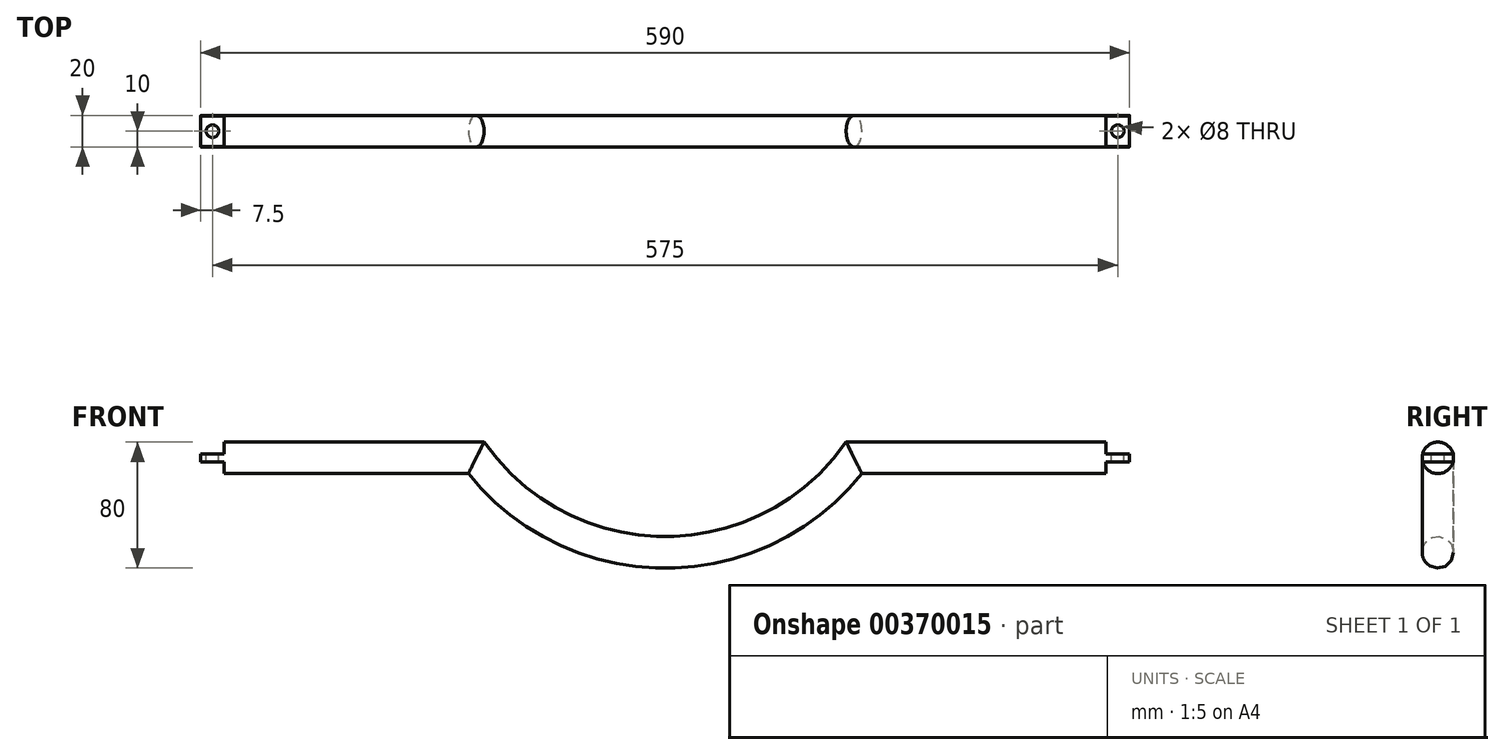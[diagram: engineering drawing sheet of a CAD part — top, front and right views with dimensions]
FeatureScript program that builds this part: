
annotation { "Feature Type Name" : "Feature", "Feature Type Description" : "" }
export const myFeature = defineFeature(function(context is Context, id is Id, definition is map)
    precondition{}
    {
        {
            var Q0;
            Q0=qCreatedBy(makeId("Front.planeOp"),FACE);
            var sketch = newSketch(context, id + "F0", { "sketchPlane" : qUnion([Q0])});
            skPoint(sketch, "E0", {"position": v(-175, 0) * mm});
            skPoint(sketch, "E1", {"position": v(-731.68, -351.24) * mm});
            skPoint(sketch, "E2", {"position": v(-590, 0) * mm});
            skPoint(sketch, "E3", {"position": v(-415, 0) * mm});
            skPoint(sketch, "E4", {"position": v(-295, -60) * mm});
            skLineSegment(sketch, "E5", {"start": v(-590, 0) * mm, "end": v(-415, 0) * mm});
            skLineSegment(sketch, "E6", {"start": v(-175, 0) * mm, "end": v(0, 0) * mm});
            skArc(sketch, "E7", {"start": v(-415, 0) * mm, "mid": v(-295, -60) * mm, "end": v(-175, 0) * mm});
            skSolve(sketch);
        }
        {
            var Q0;
            Q0=qCreatedBy(makeId("Right.planeOp"),FACE);
            var sketch = newSketch(context, id + "F1", { "sketchPlane" : qUnion([Q0])});
            skCircle(sketch, "E8", {"center": v(0, 0) * mm, "radius": 10 * mm});
            skSolve(sketch);
        }
        {
            var Q0;
            Q0=makeQuery(id+"F1.imprint","IMPRINT",FACE,{"disambiguationData":[TD([[makeQuery(id+"F1.imprint","IMPRINT",EDGE,{"derivedFrom":sQuery(id+"F1.wireOp",EDGE,"E8")}),1.0]])]});
            var Q1;
            Q1=sQuery(id+"F0.wireOp",EDGE,"E6");
            var Q2;
            Q2=sQuery(id+"F0.wireOp",EDGE,"E7");
            var Q3;
            Q3=sQuery(id+"F0.wireOp",EDGE,"E5");
            sweep(context, id + "F2", {"profiles" : qUnion([Q0]), "path" : qUnion([Q1, Q2, Q3])});
        }
        {
            var Q0;
            Q0=qCreatedBy(makeId("Front.planeOp"),FACE);
            cPlane(context, id + "F3", {"entities" : qUnion([Q0]), "cplaneType" : CPlaneType.OFFSET, "offset" : 10 * mm, "width" : 150 * mm, "height" : 150 * mm});
        }
        {
            var Q0;
            Q0=qCreatedBy(id+"F3.planeOp",FACE);
            var sketch = newSketch(context, id + "F4", { "sketchPlane" : qUnion([Q0])});
            skLineSegment(sketch, "E9.0", {"start": v(0, -10) * mm, "end": v(0, 10) * mm});
            skLineSegment(sketch, "E10", {"start": v(0, 10) * mm, "end": v(-15, 10) * mm});
            skLineSegment(sketch, "E11", {"start": v(-15, 10) * mm, "end": v(-15, -10) * mm});
            skLineSegment(sketch, "E12", {"start": v(-15, -10) * mm, "end": v(0, -10) * mm});
            skLineSegment(sketch, "E13", {"start": v(0, 0) * mm, "end": v(0, -2.5) * mm});
            skLineSegment(sketch, "E14", {"start": v(0, -2.5) * mm, "end": v(-15, -2.5) * mm});
            skLineSegment(sketch, "E15", {"start": v(-15, -2.5) * mm, "end": v(-15, 2.5) * mm});
            skLineSegment(sketch, "E16", {"start": v(-15, 2.5) * mm, "end": v(0, 2.5) * mm});
            skLineSegment(sketch, "E17", {"start": v(0, 2.5) * mm, "end": v(0, -2.5) * mm});
            skFitSpline(sketch, "E18.0", {"points": [v(-175, 0) * mm, v(-175.04, 0.08) * mm, v(-175.12, 0.23) * mm, v(-175.27, 0.54) * mm, v(-175.54, 1.09) * mm, v(-175.93, 1.85) * mm, v(-176.38, 2.76) * mm, v(-176.83, 3.65) * mm, v(-177.26, 4.52) * mm, v(-177.67, 5.34) * mm, v(-178.06, 6.13) * mm, v(-178.44, 6.87) * mm, v(-178.78, 7.56) * mm, v(-179.08, 8.17) * mm, v(-179.35, 8.7) * mm, v(-179.66, 9.32) * mm, v(-179.92, 9.85) * mm, v(-180, 10) * mm, v(-180, 10) * mm]});
            skFitSpline(sketch, "E19.0", {"points": [v(-415, 0) * mm, v(-414.96, 0.08) * mm, v(-414.88, 0.23) * mm, v(-414.73, 0.54) * mm, v(-414.46, 1.09) * mm, v(-414.07, 1.85) * mm, v(-413.62, 2.76) * mm, v(-413.17, 3.65) * mm, v(-412.74, 4.52) * mm, v(-412.33, 5.34) * mm, v(-411.94, 6.13) * mm, v(-411.56, 6.87) * mm, v(-411.22, 7.56) * mm, v(-410.92, 8.17) * mm, v(-410.65, 8.7) * mm, v(-410.34, 9.32) * mm, v(-410.08, 9.85) * mm, v(-410, 10) * mm, v(-410, 10) * mm]});
            skPoint(sketch, "E20", {"position": v(-295, 10) * mm});
            skLineSegment(sketch, "E21", {"start": v(-295, 10) * mm, "end": v(-295, -90) * mm, "construction": true});
            skLineSegment(sketch, "E22.MirrorCS", {"start": v(-590, 10) * mm, "end": v(-575, 10) * mm});
            skLineSegment(sketch, "E23.MirrorCS", {"start": v(-575, 10) * mm, "end": v(-575, -10) * mm});
            skLineSegment(sketch, "E24.MirrorCS", {"start": v(-575, 2.5) * mm, "end": v(-590, 2.5) * mm});
            skLineSegment(sketch, "E25.MirrorCS", {"start": v(-590, -2.5) * mm, "end": v(-575, -2.5) * mm});
            skLineSegment(sketch, "E26.MirrorCS", {"start": v(-575, -10) * mm, "end": v(-590, -10) * mm});
            skLineSegment(sketch, "E27.MirrorCS", {"start": v(-590, -10) * mm, "end": v(-590, 10) * mm});
            skLineSegment(sketch, "E28.MirrorCS", {"start": v(-590, 2.5) * mm, "end": v(-590, -2.5) * mm});
            skSolve(sketch);
        }
        {
            var Q0;
            {var subQ0=sQuery(id+"F4.wireOp",EDGE,"E10");Q0=makeQuery(id+"F4.imprint","IMPRINT",FACE,{"disambiguationData":[TD([[makeQuery(id+"F4.imprint","IMPRINT",EDGE,{"derivedFrom":subQ0}),1.0]])]});}
            var Q1;
            {var subQ0=sQuery(id+"F4.wireOp",EDGE,"E12");Q1=makeQuery(id+"F4.imprint","IMPRINT",FACE,{"disambiguationData":[TD([[makeQuery(id+"F4.imprint","IMPRINT",EDGE,{"derivedFrom":subQ0}),1.0]])]});}
            var Q2;
            {var subQ0=sQuery(id+"F4.wireOp",EDGE,"E22.MirrorCS");Q2=makeQuery(id+"F4.imprint","IMPRINT",FACE,{"disambiguationData":[TD([[makeQuery(id+"F4.imprint","IMPRINT",EDGE,{"derivedFrom":subQ0}),-1.0]])]});}
            var Q3;
            {var subQ2=sQuery(id+"F4.wireOp",EDGE,"E25.MirrorCS");Q3=makeQuery(id+"F4.imprint","IMPRINT",FACE,{"disambiguationData":[TD([[makeQuery(id+"F4.imprint","IMPRINT",EDGE,{"derivedFrom":subQ2}),-1.0]])]});}
            extrude(context, id + "F5", {"entities" : qUnion([Q0, Q1, Q2, Q3]), "operationType" : NewBodyOperationType.REMOVE, "oppositeDirection" : true, "depth" : 20 * mm});
        }
        {
            var Q0;
            Q0=makeQuery(id+"F5.boolean.opBoolean","COPY",FACE,{"derivedFrom":makeQuery(id+"F5.opExtrude","SWEPT_FACE",FACE,{"disambiguationData":[OSD([sQuery(id+"F4.wireOp",EDGE,"E16")])]})});
            var sketch = newSketch(context, id + "F6", { "sketchPlane" : qUnion([Q0])});
            skPoint(sketch, "E29", {"position": v(-7.5, 0) * mm});
            skPoint(sketch, "E29.positionSnap0", {"position": v(-7.5, 9.68) * mm});
            skCircle(sketch, "E30", {"center": v(-7.5, 0) * mm, "radius": 4 * mm});
            skLineSegment(sketch, "E31.0", {"start": v(-590, 9.68) * mm, "end": v(-590, -9.68) * mm});
            skPoint(sketch, "E32", {"position": v(-582.5, 0) * mm});
            skPoint(sketch, "E32.positionSnap0", {"position": v(-590, 0) * mm});
            skCircle(sketch, "E33", {"center": v(-582.5, 0) * mm, "radius": 4 * mm});
            skSolve(sketch);
        }
        {
            var Q0;
            Q0=qSketchRegion(id+"F6",true);
            extrude(context, id + "F7", {"entities" : qUnion([Q0]), "operationType" : NewBodyOperationType.REMOVE, "oppositeDirection" : true, "depth" : 5 * mm});
        }
    });
